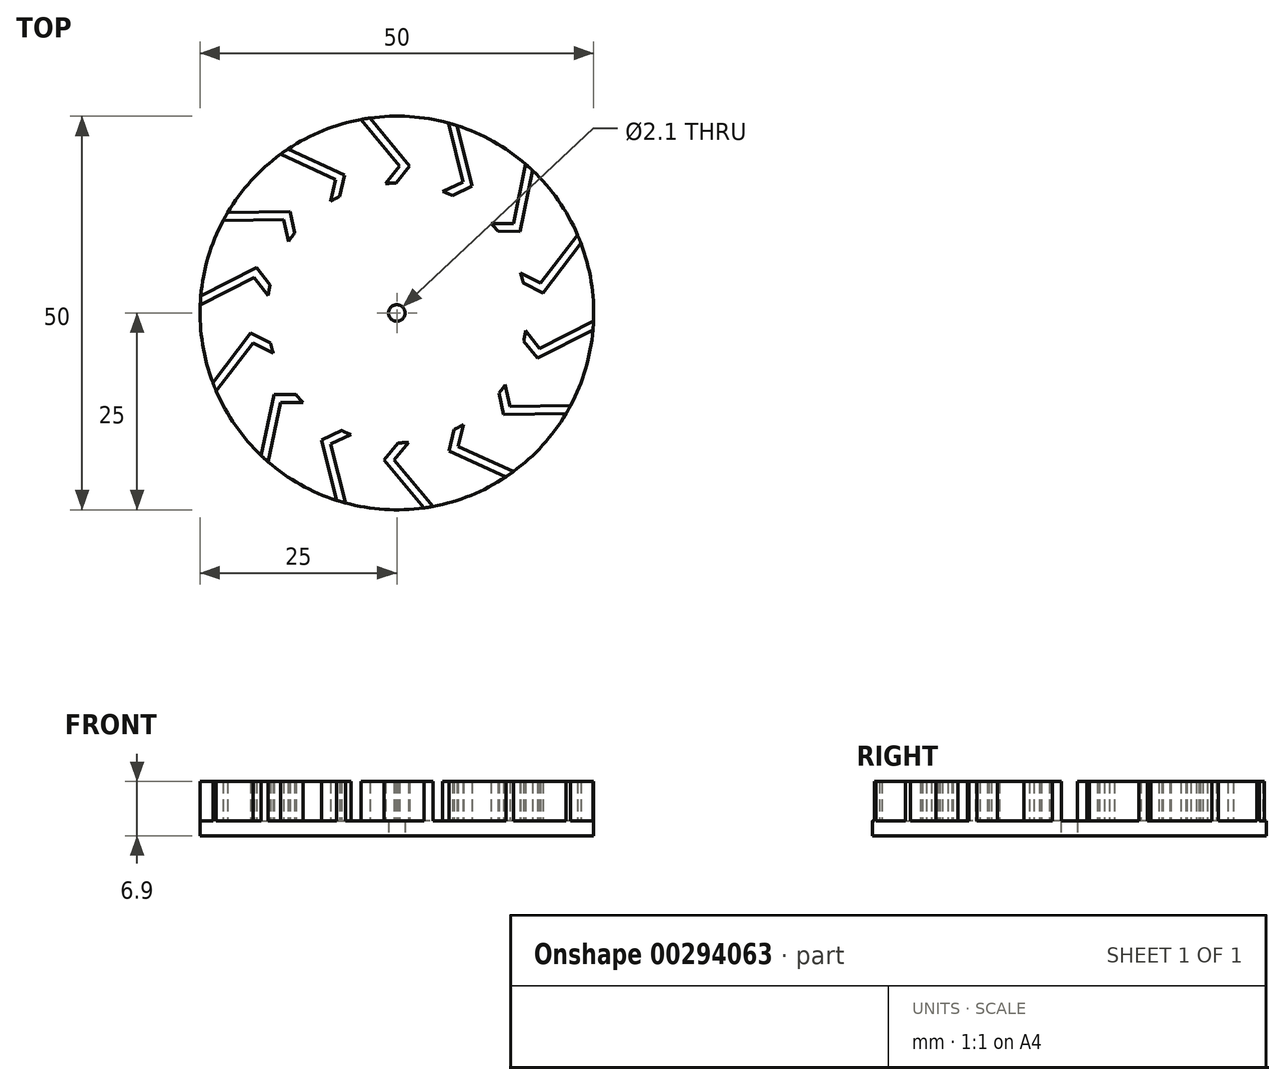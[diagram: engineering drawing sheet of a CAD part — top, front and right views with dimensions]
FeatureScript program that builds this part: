
annotation { "Feature Type Name" : "Feature", "Feature Type Description" : "" }
export const myFeature = defineFeature(function(context is Context, id is Id, definition is map)
    precondition{}
    {
        {
            var Q0;
            Q0=qCreatedBy(makeId("Top.planeOp"),FACE);
            var sketch = newSketch(context, id + "F0", { "sketchPlane" : qUnion([Q0])});
            skCircle(sketch, "E0", {"center": v(0, 0) * mm, "radius": 25 * mm});
            skSolve(sketch);
        }
        {
            var Q0;
            Q0=makeQuery(id+"F0.imprint","IMPRINT",FACE,{"disambiguationData":[TD([[makeQuery(id+"F0.imprint","IMPRINT",EDGE,{"derivedFrom":sQuery(id+"F0.wireOp",EDGE,"E0")}),1.0]])]});
            var Q1;
            Q1=sQuery(id+"F0.wireOp",EDGE,"E0");
            extrude(context, id + "F1", {"entities" : qUnion([Q0]), "surfaceEntities" : qUnion([Q1]), "depth" : 1.9 * mm});
        }
        {
            var Q0;
            Q0=qCreatedBy(makeId("Top.planeOp"),FACE);
            var sketch = newSketch(context, id + "F2", { "sketchPlane" : qUnion([Q0])});
            skCircle(sketch, "E1", {"center": v(0, 0) * mm, "radius": 1.05 * mm});
            skSolve(sketch);
        }
        {
            var Q0;
            Q0=makeQuery(id+"F2.imprint","IMPRINT",FACE,{"disambiguationData":[TD([[makeQuery(id+"F2.imprint","IMPRINT",EDGE,{"derivedFrom":sQuery(id+"F2.wireOp",EDGE,"E1")}),1.0]])]});
            var Q1;
            Q1=sQuery(id+"F2.wireOp",EDGE,"E1");
            extrude(context, id + "F3", {"entities" : qUnion([Q0]), "operationType" : NewBodyOperationType.REMOVE, "surfaceEntities" : qUnion([Q1]), "depth" : 25.4 * mm});
        }
        {
            var Q0;
            Q0=makeQuery(id+"F1.opExtrude","CAP_FACE",FACE,{"disambiguationData":[OSD([sQuery(id+"F0.wireOp",EDGE,"E0")])],"isStart":false});
            var sketch = newSketch(context, id + "F4", { "sketchPlane" : qUnion([Q0])});
            skCircle(sketch, "E2", {"center": v(0, 0) * mm, "radius": 16.5 * mm});
            skLineSegment(sketch, "E3", {"start": v(-3.43, 24.76) * mm, "end": v(1.63, 18.67) * mm});
            skLineSegment(sketch, "E4", {"start": v(1.63, 18.67) * mm, "end": v(-0.12, 16.5) * mm});
            skLineSegment(sketch, "E5", {"start": v(-4.58, 24.58) * mm, "end": v(0.34, 18.66) * mm});
            skPoint(sketch, "E5.endSnap0", {"position": v(0, 21.9) * mm});
            skLineSegment(sketch, "E6", {"start": v(0.34, 18.66) * mm, "end": v(-1.46, 16.44) * mm});
            skLineSegment(sketch, "E7.1.0", {"start": v(-13.84, 20.82) * mm, "end": v(-6.63, 17.52) * mm});
            skLineSegment(sketch, "E7.1.1", {"start": v(-14.79, 20.16) * mm, "end": v(-7.79, 16.96) * mm});
            skLineSegment(sketch, "E7.1.2", {"start": v(-7.79, 16.96) * mm, "end": v(-8.44, 14.18) * mm});
            skLineSegment(sketch, "E7.1.3", {"start": v(-6.63, 17.52) * mm, "end": v(-7.27, 14.81) * mm});
            skLineSegment(sketch, "E7.2.0", {"start": v(-21.5, 12.76) * mm, "end": v(-13.58, 12.91) * mm});
            skLineSegment(sketch, "E7.2.1", {"start": v(-22.07, 11.75) * mm, "end": v(-14.38, 11.9) * mm});
            skLineSegment(sketch, "E7.2.2", {"start": v(-14.38, 11.9) * mm, "end": v(-13.76, 9.1) * mm});
            skLineSegment(sketch, "E7.2.3", {"start": v(-13.58, 12.91) * mm, "end": v(-12.97, 10.2) * mm});
            skLineSegment(sketch, "E7.3.0", {"start": v(-24.9, 2.17) * mm, "end": v(-17.83, 5.74) * mm});
            skLineSegment(sketch, "E7.3.1", {"start": v(-24.98, 1) * mm, "end": v(-18.11, 4.48) * mm});
            skLineSegment(sketch, "E7.3.2", {"start": v(-18.11, 4.48) * mm, "end": v(-16.35, 2.24) * mm});
            skLineSegment(sketch, "E7.3.3", {"start": v(-17.83, 5.74) * mm, "end": v(-16.11, 3.55) * mm});
            skLineSegment(sketch, "E7.4.0", {"start": v(-23.38, -8.86) * mm, "end": v(-18.56, -2.56) * mm});
            skLineSegment(sketch, "E7.4.1", {"start": v(-22.94, -9.93) * mm, "end": v(-18.26, -3.82) * mm});
            skLineSegment(sketch, "E7.4.2", {"start": v(-18.26, -3.82) * mm, "end": v(-15.7, -5.08) * mm});
            skLineSegment(sketch, "E7.4.3", {"start": v(-18.56, -2.56) * mm, "end": v(-16.06, -3.79) * mm});
            skLineSegment(sketch, "E7.5.0", {"start": v(-17.22, -18.12) * mm, "end": v(-15.61, -10.36) * mm});
            skLineSegment(sketch, "E7.5.1", {"start": v(-16.36, -18.9) * mm, "end": v(-14.8, -11.37) * mm});
            skLineSegment(sketch, "E7.5.2", {"start": v(-14.8, -11.37) * mm, "end": v(-11.94, -11.39) * mm});
            skLineSegment(sketch, "E7.5.3", {"start": v(-15.61, -10.36) * mm, "end": v(-12.82, -10.38) * mm});
            skLineSegment(sketch, "E7.6.0", {"start": v(-7.65, -23.8) * mm, "end": v(-9.57, -16.1) * mm});
            skLineSegment(sketch, "E7.6.1", {"start": v(-6.54, -24.13) * mm, "end": v(-8.4, -16.66) * mm});
            skLineSegment(sketch, "E7.6.2", {"start": v(-8.4, -16.66) * mm, "end": v(-5.82, -15.44) * mm});
            skLineSegment(sketch, "E7.6.3", {"start": v(-9.57, -16.1) * mm, "end": v(-7.05, -14.92) * mm});
            skLineSegment(sketch, "E7.7.0", {"start": v(3.43, -24.76) * mm, "end": v(-1.63, -18.67) * mm});
            skLineSegment(sketch, "E7.7.1", {"start": v(4.58, -24.58) * mm, "end": v(-0.34, -18.66) * mm});
            skLineSegment(sketch, "E7.7.2", {"start": v(-0.34, -18.66) * mm, "end": v(1.46, -16.44) * mm});
            skLineSegment(sketch, "E7.7.3", {"start": v(-1.63, -18.67) * mm, "end": v(0.12, -16.5) * mm});
            skLineSegment(sketch, "E7.8.0", {"start": v(13.84, -20.82) * mm, "end": v(6.63, -17.52) * mm});
            skLineSegment(sketch, "E7.8.1", {"start": v(14.79, -20.16) * mm, "end": v(7.79, -16.96) * mm});
            skLineSegment(sketch, "E7.8.2", {"start": v(7.79, -16.96) * mm, "end": v(8.44, -14.18) * mm});
            skLineSegment(sketch, "E7.8.3", {"start": v(6.63, -17.52) * mm, "end": v(7.27, -14.81) * mm});
            skLineSegment(sketch, "E7.9.0", {"start": v(21.5, -12.76) * mm, "end": v(13.58, -12.91) * mm});
            skLineSegment(sketch, "E7.9.1", {"start": v(22.07, -11.75) * mm, "end": v(14.38, -11.9) * mm});
            skLineSegment(sketch, "E7.9.2", {"start": v(14.38, -11.9) * mm, "end": v(13.76, -9.1) * mm});
            skLineSegment(sketch, "E7.9.3", {"start": v(13.58, -12.91) * mm, "end": v(12.97, -10.2) * mm});
            skLineSegment(sketch, "E7.10.0", {"start": v(24.9, -2.17) * mm, "end": v(17.83, -5.74) * mm});
            skLineSegment(sketch, "E7.10.1", {"start": v(24.98, -1) * mm, "end": v(18.11, -4.48) * mm});
            skLineSegment(sketch, "E7.10.2", {"start": v(18.11, -4.48) * mm, "end": v(16.35, -2.24) * mm});
            skLineSegment(sketch, "E7.10.3", {"start": v(17.83, -5.74) * mm, "end": v(16.11, -3.55) * mm});
            skLineSegment(sketch, "E7.11.0", {"start": v(23.38, 8.86) * mm, "end": v(18.56, 2.56) * mm});
            skLineSegment(sketch, "E7.11.1", {"start": v(22.94, 9.93) * mm, "end": v(18.26, 3.82) * mm});
            skLineSegment(sketch, "E7.11.2", {"start": v(18.26, 3.82) * mm, "end": v(15.7, 5.08) * mm});
            skLineSegment(sketch, "E7.11.3", {"start": v(18.56, 2.56) * mm, "end": v(16.06, 3.79) * mm});
            skLineSegment(sketch, "E7.12.0", {"start": v(17.22, 18.12) * mm, "end": v(15.61, 10.36) * mm});
            skLineSegment(sketch, "E7.12.1", {"start": v(16.36, 18.9) * mm, "end": v(14.8, 11.37) * mm});
            skLineSegment(sketch, "E7.12.2", {"start": v(14.8, 11.37) * mm, "end": v(11.94, 11.39) * mm});
            skLineSegment(sketch, "E7.12.3", {"start": v(15.61, 10.36) * mm, "end": v(12.82, 10.38) * mm});
            skLineSegment(sketch, "E7.13.0", {"start": v(7.65, 23.8) * mm, "end": v(9.57, 16.1) * mm});
            skLineSegment(sketch, "E7.13.1", {"start": v(6.54, 24.13) * mm, "end": v(8.4, 16.66) * mm});
            skLineSegment(sketch, "E7.13.2", {"start": v(8.4, 16.66) * mm, "end": v(5.82, 15.44) * mm});
            skLineSegment(sketch, "E7.13.3", {"start": v(9.57, 16.1) * mm, "end": v(7.05, 14.92) * mm});
            skSolve(sketch);
        }
        {
            var Q0;
            {var subQ1=sQuery(id+"F4.wireOp",EDGE,"E7.1.0");Q0=makeQuery(id+"F4.imprint","IMPRINT",FACE,{"disambiguationData":[TD([[makeQuery(id+"F4.imprint","IMPRINT",EDGE,{"derivedFrom":subQ1}),-1.0]])]});}
            var Q1;
            {var subQ1=sQuery(id+"F4.wireOp",EDGE,"E3");Q1=makeQuery(id+"F4.imprint","IMPRINT",FACE,{"disambiguationData":[TD([[makeQuery(id+"F4.imprint","IMPRINT",EDGE,{"derivedFrom":subQ1}),-1.0]])]});}
            var Q2;
            {var subQ4=sQuery(id+"F4.wireOp",EDGE,"E7.13.0");Q2=makeQuery(id+"F4.imprint","IMPRINT",FACE,{"disambiguationData":[TD([[makeQuery(id+"F4.imprint","IMPRINT",EDGE,{"derivedFrom":subQ4}),-1.0]])]});}
            var Q3;
            {var subQ1=sQuery(id+"F4.wireOp",EDGE,"E7.12.0");Q3=makeQuery(id+"F4.imprint","IMPRINT",FACE,{"disambiguationData":[TD([[makeQuery(id+"F4.imprint","IMPRINT",EDGE,{"derivedFrom":subQ1}),-1.0]])]});}
            var Q4;
            {var subQ2=sQuery(id+"F4.wireOp",EDGE,"E7.11.0");Q4=makeQuery(id+"F4.imprint","IMPRINT",FACE,{"disambiguationData":[TD([[makeQuery(id+"F4.imprint","IMPRINT",EDGE,{"derivedFrom":subQ2}),-1.0]])]});}
            var Q5;
            {var subQ4=sQuery(id+"F4.wireOp",EDGE,"E7.10.0");Q5=makeQuery(id+"F4.imprint","IMPRINT",FACE,{"disambiguationData":[TD([[makeQuery(id+"F4.imprint","IMPRINT",EDGE,{"derivedFrom":subQ4}),-1.0]])]});}
            var Q6;
            {var subQ2=sQuery(id+"F4.wireOp",EDGE,"E7.9.0");Q6=makeQuery(id+"F4.imprint","IMPRINT",FACE,{"disambiguationData":[TD([[makeQuery(id+"F4.imprint","IMPRINT",EDGE,{"derivedFrom":subQ2}),-1.0]])]});}
            var Q7;
            {var subQ1=sQuery(id+"F4.wireOp",EDGE,"E7.8.0");Q7=makeQuery(id+"F4.imprint","IMPRINT",FACE,{"disambiguationData":[TD([[makeQuery(id+"F4.imprint","IMPRINT",EDGE,{"derivedFrom":subQ1}),-1.0]])]});}
            var Q8;
            {var subQ2=sQuery(id+"F4.wireOp",EDGE,"E7.7.0");Q8=makeQuery(id+"F4.imprint","IMPRINT",FACE,{"disambiguationData":[TD([[makeQuery(id+"F4.imprint","IMPRINT",EDGE,{"derivedFrom":subQ2}),-1.0]])]});}
            var Q9;
            {var subQ1=sQuery(id+"F4.wireOp",EDGE,"E7.6.0");Q9=makeQuery(id+"F4.imprint","IMPRINT",FACE,{"disambiguationData":[TD([[makeQuery(id+"F4.imprint","IMPRINT",EDGE,{"derivedFrom":subQ1}),-1.0]])]});}
            var Q10;
            {var subQ4=sQuery(id+"F4.wireOp",EDGE,"E7.5.0");Q10=makeQuery(id+"F4.imprint","IMPRINT",FACE,{"disambiguationData":[TD([[makeQuery(id+"F4.imprint","IMPRINT",EDGE,{"derivedFrom":subQ4}),-1.0]])]});}
            var Q11;
            {var subQ2=sQuery(id+"F4.wireOp",EDGE,"E7.4.0");Q11=makeQuery(id+"F4.imprint","IMPRINT",FACE,{"disambiguationData":[TD([[makeQuery(id+"F4.imprint","IMPRINT",EDGE,{"derivedFrom":subQ2}),-1.0]])]});}
            var Q12;
            {var subQ1=sQuery(id+"F4.wireOp",EDGE,"E7.3.0");Q12=makeQuery(id+"F4.imprint","IMPRINT",FACE,{"disambiguationData":[TD([[makeQuery(id+"F4.imprint","IMPRINT",EDGE,{"derivedFrom":subQ1}),-1.0]])]});}
            var Q13;
            {var subQ2=sQuery(id+"F4.wireOp",EDGE,"E7.2.0");Q13=makeQuery(id+"F4.imprint","IMPRINT",FACE,{"disambiguationData":[TD([[makeQuery(id+"F4.imprint","IMPRINT",EDGE,{"derivedFrom":subQ2}),-1.0]])]});}
            extrude(context, id + "F5", {"entities" : qUnion([Q0, Q1, Q2, Q3, Q4, Q5, Q6, Q7, Q8, Q9, Q10, Q11, Q12, Q13]), "operationType" : NewBodyOperationType.ADD, "depth" : 5 * mm});
        }
    });
